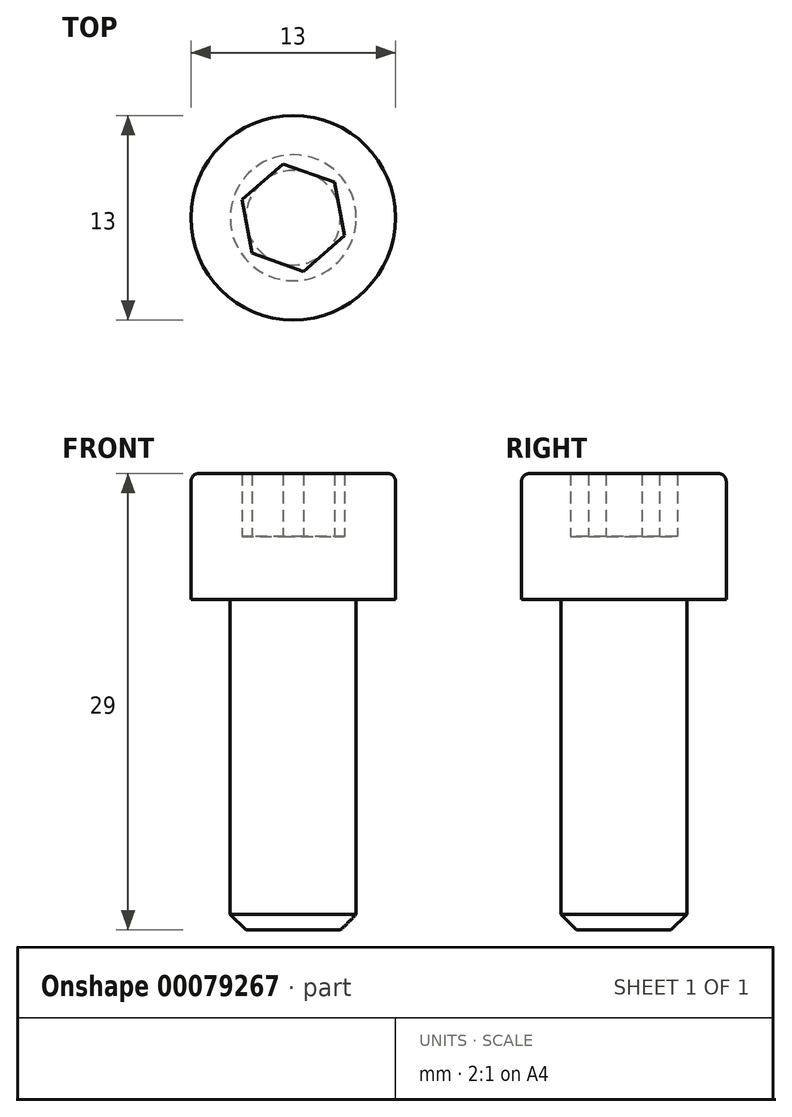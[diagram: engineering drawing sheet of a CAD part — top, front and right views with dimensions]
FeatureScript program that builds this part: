
annotation { "Feature Type Name" : "Feature", "Feature Type Description" : "" }
export const myFeature = defineFeature(function(context is Context, id is Id, definition is map)
    precondition{}
    {
        {
            var Q0;
            Q0=qCreatedBy(makeId("Top.planeOp"),FACE);
            var sketch = newSketch(context, id + "F0", { "sketchPlane" : qUnion([Q0])});
            skCircle(sketch, "E0", {"center": v(0, 0) * mm, "radius": 4 * mm});
            skCircle(sketch, "E1.cCircle", {"center": v(0, 0) * mm, "radius": 3 * mm, "construction": true});
            skLineSegment(sketch, "E1.0", {"start": v(-3.27, 1.15) * mm, "end": v(-0.64, 3.4) * mm});
            skLineSegment(sketch, "E1.1", {"start": v(-0.64, 3.4) * mm, "end": v(2.63, 2.26) * mm});
            skLineSegment(sketch, "E1.2", {"start": v(2.63, 2.26) * mm, "end": v(3.27, -1.15) * mm});
            skLineSegment(sketch, "E1.3", {"start": v(3.27, -1.15) * mm, "end": v(0.64, -3.4) * mm});
            skLineSegment(sketch, "E1.4", {"start": v(0.64, -3.4) * mm, "end": v(-2.63, -2.26) * mm});
            skLineSegment(sketch, "E1.5", {"start": v(-2.63, -2.26) * mm, "end": v(-3.27, 1.15) * mm});
            skPoint(sketch, "E1.0.midPoint", {"position": v(-1.96, 2.28) * mm});
            skCircle(sketch, "E2", {"center": v(0, 0) * mm, "radius": 6.5 * mm});
            skSolve(sketch);
        }
        {
            var Q0;
            Q0 = qSketchRegion(id + "F0", true);
            var Q1;
            Q1=makeQuery(id+"F0.imprint","IMPRINT",FACE,{"disambiguationData":[TD([[makeQuery(id+"F0.imprint","IMPRINT",EDGE,{"derivedFrom":sQuery(id+"F0.wireOp",EDGE,"E0")}),1.0]])]});
            var Q2;
            Q2=makeQuery(id+"F0.imprint","IMPRINT",FACE,{"disambiguationData":[TD([[makeQuery(id+"F0.imprint","IMPRINT",EDGE,{"derivedFrom":sQuery(id+"F0.wireOp",EDGE,"E1.0")}),-1.0]])]});
            extrude(context, id + "F1", {"entities" : qUnion([Q0, Q1, Q2]), "oppositeDirection" : true, "depth" : 4 * mm});
        }
        {
            var Q0;
            Q0=makeQuery(id+"F0.imprint","IMPRINT",FACE,{"disambiguationData":[TD([[makeQuery(id+"F0.imprint","IMPRINT",EDGE,{"derivedFrom":sQuery(id+"F0.wireOp",EDGE,"E0")}),1.0]])]});
            var Q1;
            Q1=makeQuery(id+"F0.imprint","IMPRINT",FACE,{"disambiguationData":[TD([[makeQuery(id+"F0.imprint","IMPRINT",EDGE,{"derivedFrom":sQuery(id+"F0.wireOp",EDGE,"E0")}),-1.0]])]});
            extrude(context, id + "F2", {"entities" : qUnion([Q0, Q1]), "operationType" : NewBodyOperationType.ADD, "depth" : 4 * mm});
        }
        {
            var Q0;
            Q0=makeQuery(id+"F0.imprint","IMPRINT",FACE,{"disambiguationData":[TD([[makeQuery(id+"F0.imprint","IMPRINT",EDGE,{"derivedFrom":sQuery(id+"F0.wireOp",EDGE,"E1.0")}),-1.0]])]});
            var Q1;
            Q1=makeQuery(id+"F0.imprint","IMPRINT",FACE,{"disambiguationData":[TD([[makeQuery(id+"F0.imprint","IMPRINT",EDGE,{"derivedFrom":sQuery(id+"F0.wireOp",EDGE,"E0")}),1.0]])]});
            extrude(context, id + "F3", {"entities" : qUnion([Q0, Q1]), "operationType" : NewBodyOperationType.ADD, "oppositeDirection" : true, "depth" : 25 * mm});
        }
        {
            var Q0;
            Q0=makeQuery(id+"F2.opExtrude","CAP_EDGE",EDGE,{"disambiguationData":[OSD([sQuery(id+"F0.wireOp",EDGE,"E2")])],"isStart":false});
            fillet(context, id + "F4", {"entities" : qUnion([Q0]), "radius" : 0.5 * mm, "tangentPropagation" : true, "allowEdgeOverflow" : false});
        }
        {
            var Q0;
            Q0=makeQuery(id+"F3.opExtrude","CAP_FACE",FACE,{"disambiguationData":[OSD([sQuery(id+"F0.wireOp",EDGE,"E0")])],"isStart":false});
            chamfer(context, id + "F5", {"entities" : qUnion([Q0]), "width" : 1 * mm, "tangentPropagation" : true});
        }
    });
